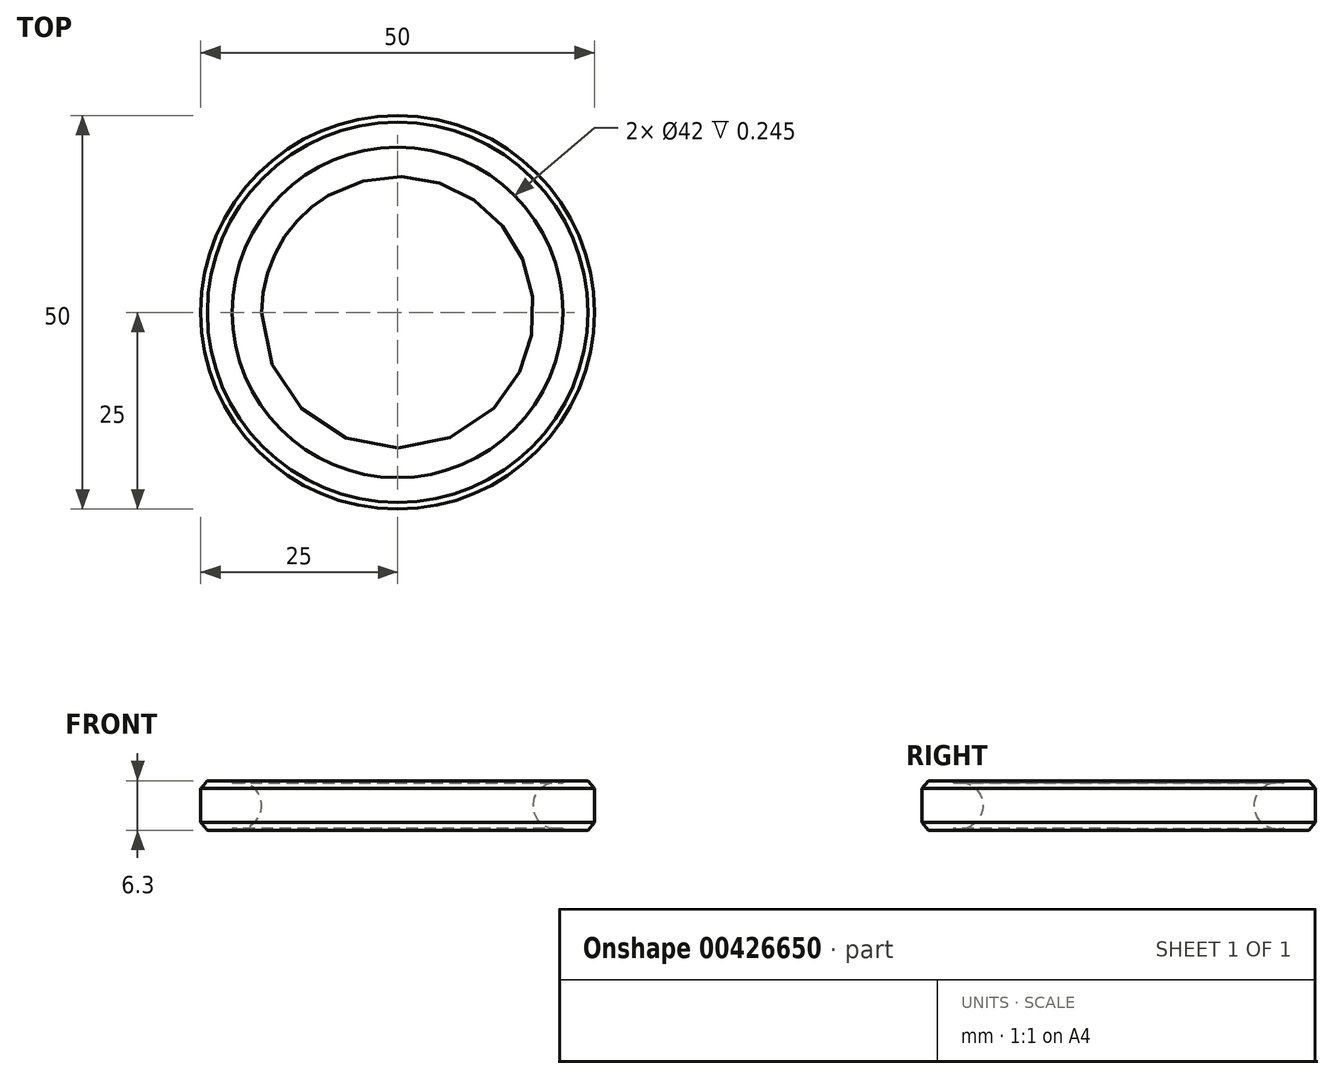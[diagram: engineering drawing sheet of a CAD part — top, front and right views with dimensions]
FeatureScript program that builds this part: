
annotation { "Feature Type Name" : "Feature", "Feature Type Description" : "" }
export const myFeature = defineFeature(function(context is Context, id is Id, definition is map)
    precondition{}
    {
        {
            var Q0;
            Q0=qCreatedBy(makeId("Right.planeOp"),FACE);
            var sketch = newSketch(context, id + "F0", { "sketchPlane" : qUnion([Q0])});
            skCircle(sketch, "E0", {"center": v(-20.25, 0) * mm, "radius": 3 * mm});
            skLineSegment(sketch, "E1", {"start": v(0, 0) * mm, "end": v(0, 7.06) * mm, "construction": true});
            skLineSegment(sketch, "E2", {"start": v(0, 0) * mm, "end": v(-17.25, 0) * mm, "construction": true});
            skSolve(sketch);
        }
        {
            var Q0;
            Q0=qCreatedBy(makeId("Right.planeOp"),FACE);
            var sketch = newSketch(context, id + "F1", { "sketchPlane" : qUnion([Q0])});
            skLineSegment(sketch, "E3", {"start": v(-21, 3.15) * mm, "end": v(-21, -3.15) * mm});
            skLineSegment(sketch, "E4", {"start": v(-21, -3.15) * mm, "end": v(-24.16, -3.15) * mm});
            skLineSegment(sketch, "E5", {"start": v(-24.16, -3.15) * mm, "end": v(-25, -2.15) * mm});
            skLineSegment(sketch, "E6", {"start": v(-25, -2.15) * mm, "end": v(-25, 2.15) * mm});
            skLineSegment(sketch, "E7", {"start": v(-25, 2.15) * mm, "end": v(-24.16, 3.15) * mm});
            skLineSegment(sketch, "E8", {"start": v(-24.16, 3.15) * mm, "end": v(-21, 3.15) * mm});
            skLineSegment(sketch, "E9", {"start": v(-21, 0) * mm, "end": v(-22.44, 0) * mm, "construction": true});
            skLineSegment(sketch, "E10", {"start": v(-23.25, 0) * mm, "end": v(-21, 0) * mm, "construction": true});
            skLineSegment(sketch, "E11", {"start": v(0, 0) * mm, "end": v(0, 8.7) * mm, "construction": true});
            skSolve(sketch);
        }
        {
            var Q0;
            Q0 = qSketchRegion(id + "F0", true);
            var Q1;
            Q1=sQuery(id+"F0.wireOp",EDGE,"E1");
            revolve(context, id + "F2", {"surfaceOperationType" : NewSurfaceOperationType.NEW, "entities" : qUnion([Q0]), "axis" : qUnion([Q1]), "revolveType" : RevolveType.FULL});
        }
        {
            var Q0;
            Q0 = qSketchRegion(id + "F1", true);
            var Q1;
            Q1=sQuery(id+"F1.wireOp",EDGE,"E11");
            revolve(context, id + "F3", {"operationType" : NewBodyOperationType.ADD, "surfaceOperationType" : NewSurfaceOperationType.NEW, "entities" : qUnion([Q0]), "axis" : qUnion([Q1]), "revolveType" : RevolveType.FULL});
        }
    });
